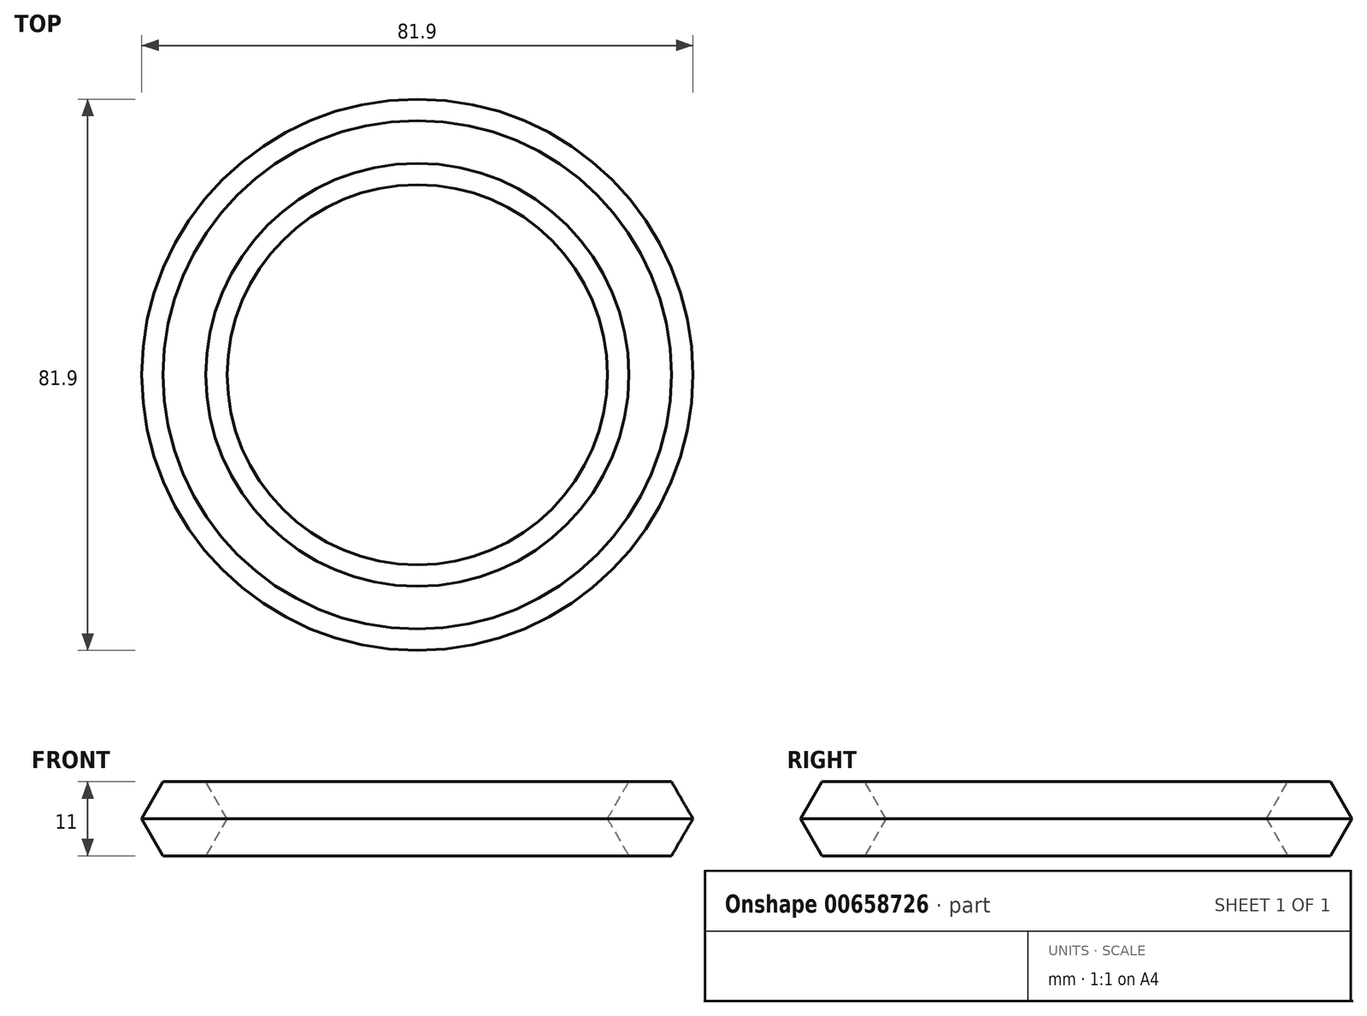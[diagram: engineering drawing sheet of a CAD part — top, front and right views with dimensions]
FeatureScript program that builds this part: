
annotation { "Feature Type Name" : "Feature", "Feature Type Description" : "" }
export const myFeature = defineFeature(function(context is Context, id is Id, definition is map)
    precondition{}
    {
        {
            var Q0;
            Q0=qCreatedBy(makeId("Top.planeOp"),FACE);
            var sketch = newSketch(context, id + "F0", { "sketchPlane" : qUnion([Q0])});
            skCircle(sketch, "E0", {"center": v(0, 0) * mm, "radius": 34.6 * mm});
            skSolve(sketch);
        }
        {
            var Q0;
            Q0=qCreatedBy(makeId("Front.planeOp"),FACE);
            var sketch = newSketch(context, id + "F1", { "sketchPlane" : qUnion([Q0])});
            skLineSegment(sketch, "E1.0", {"start": v(-34.6, 0) * mm, "end": v(34.6, 0) * mm, "construction": true});
            skCircle(sketch, "E2.cCircle", {"center": v(34.6, 0) * mm, "radius": 6.35 * mm, "construction": true});
            skLineSegment(sketch, "E2.0", {"start": v(28.25, 0) * mm, "end": v(31.43, 5.5) * mm});
            skLineSegment(sketch, "E2.1", {"start": v(31.43, 5.5) * mm, "end": v(37.78, 5.5) * mm});
            skLineSegment(sketch, "E2.2", {"start": v(37.78, 5.5) * mm, "end": v(40.95, 0) * mm});
            skLineSegment(sketch, "E2.3", {"start": v(40.95, 0) * mm, "end": v(37.78, -5.5) * mm});
            skLineSegment(sketch, "E2.4", {"start": v(37.78, -5.5) * mm, "end": v(31.43, -5.5) * mm});
            skLineSegment(sketch, "E2.5", {"start": v(31.43, -5.5) * mm, "end": v(28.25, 0) * mm});
            skSolve(sketch);
        }
        {
            var Q0;
            Q0=makeQuery(id+"F1.imprint","IMPRINT",FACE,{"disambiguationData":[TD([[makeQuery(id+"F1.imprint","IMPRINT",EDGE,{"derivedFrom":sQuery(id+"F1.wireOp",EDGE,"E2.0")}),-1.0]])]});
            var Q1;
            Q1=sQuery(id+"F0.wireOp",EDGE,"E0");
            sweep(context, id + "F2", {"profiles" : qUnion([Q0]), "path" : qUnion([Q1])});
        }
    });
